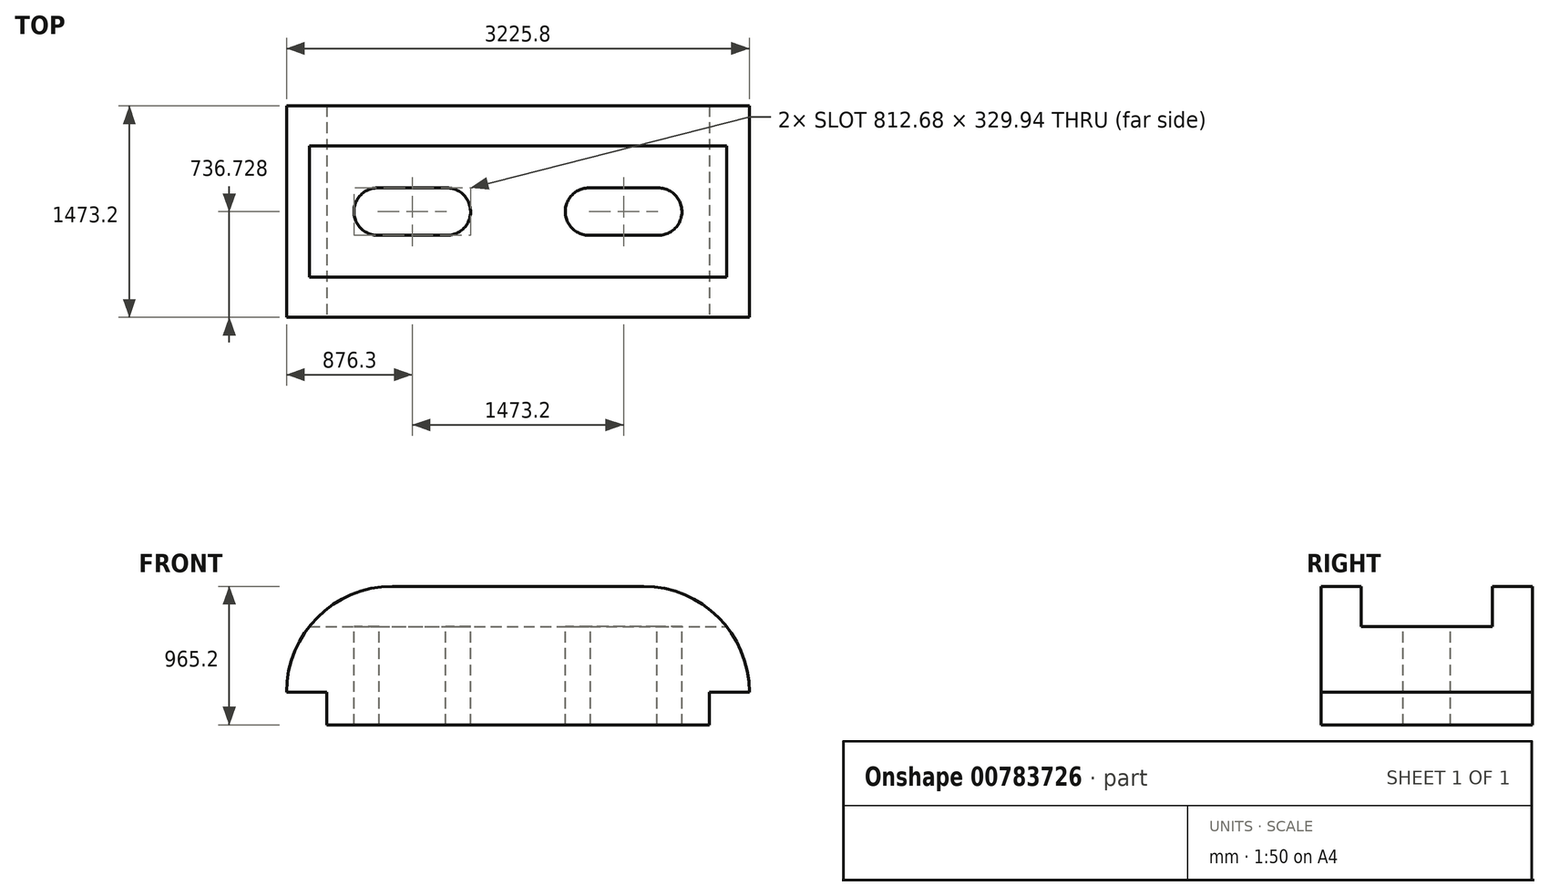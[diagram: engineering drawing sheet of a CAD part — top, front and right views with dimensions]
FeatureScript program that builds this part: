
annotation { "Feature Type Name" : "Feature", "Feature Type Description" : "" }
export const myFeature = defineFeature(function(context is Context, id is Id, definition is map)
    precondition{}
    {
        {
            var Q0;
            Q0=qCreatedBy(makeId("Front.planeOp"),FACE);
            var sketch = newSketch(context, id + "F0", { "sketchPlane" : qUnion([Q0])});
            skLineSegment(sketch, "E0.bottom", {"start": v(1612.9, 482.6) * mm, "end": v(-1612.9, 482.6) * mm});
            skLineSegment(sketch, "E0.top", {"start": v(1612.9, -482.6) * mm, "end": v(-1612.9, -482.6) * mm});
            skLineSegment(sketch, "E0.left", {"start": v(1612.9, 482.6) * mm, "end": v(1612.9, -482.6) * mm});
            skLineSegment(sketch, "E0.right", {"start": v(-1612.9, 482.6) * mm, "end": v(-1612.9, -482.6) * mm});
            skPoint(sketch, "E0.middle", {"position": v(0, 0) * mm});
            skSolve(sketch);
        }
        {
            var Q0;
            Q0=qSketchRegion(id+"F0",true);
            extrude(context, id + "F1", {"entities" : qUnion([Q0]), "depth" : 1473.2 * mm});
        }
        {
            var Q0;
            Q0=makeQuery(id+"F1.opExtrude","SWEPT_FACE",FACE,{"disambiguationData":[OSD([sQuery(id+"F0.wireOp",EDGE,"E0.bottom")])]});
            var sketch = newSketch(context, id + "F2", { "sketchPlane" : qUnion([Q0])});
            skArc(sketch, "E1", {"start": v(-977.59, -571.5) * mm, "mid": v(-1142.94, -741.04) * mm, "end": v(-968.7, -901.44) * mm});
            skPoint(sketch, "E1.centerSnap0", {"position": v(-1612.9, -736.6) * mm});
            skArc(sketch, "E2", {"start": v(-504.5, -901.44) * mm, "mid": v(-330.26, -741.04) * mm, "end": v(-495.61, -571.5) * mm});
            skLineSegment(sketch, "E3", {"start": v(-977.59, -571.5) * mm, "end": v(-494.99, -571.5) * mm});
            skLineSegment(sketch, "E4", {"start": v(-968.7, -901.44) * mm, "end": v(-486.1, -901.44) * mm});
            skLineSegment(sketch, "E5.MirrorCS", {"start": v(977.59, -571.5) * mm, "end": v(494.99, -571.5) * mm});
            skArc(sketch, "E6.MirrorCS", {"start": v(977.59, -571.5) * mm, "mid": v(1142.94, -741.04) * mm, "end": v(968.7, -901.44) * mm});
            skLineSegment(sketch, "E7.MirrorCS", {"start": v(968.7, -901.44) * mm, "end": v(486.1, -901.44) * mm});
            skArc(sketch, "E8.MirrorCS", {"start": v(504.5, -901.44) * mm, "mid": v(330.26, -741.04) * mm, "end": v(495.61, -571.5) * mm});
            skSolve(sketch);
        }
        {
            var Q0;
            Q0=qSketchRegion(id+"F2",true);
            extrude(context, id + "F3", {"entities" : qUnion([Q0]), "operationType" : NewBodyOperationType.REMOVE, "endBound" : BoundingType.THROUGH_ALL, "oppositeDirection" : true, "depth" : 25.4 * mm});
        }
        {
            var Q0;
            Q0=makeQuery(id+"F1.opExtrude","SWEPT_FACE",FACE,{"disambiguationData":[OSD([sQuery(id+"F0.wireOp",EDGE,"E0.left")])]});
            var sketch = newSketch(context, id + "F4", { "sketchPlane" : qUnion([Q0])});
            skLineSegment(sketch, "E9.bottom", {"start": v(-1193.8, 482.6) * mm, "end": v(-279.4, 482.6) * mm});
            skLineSegment(sketch, "E9.top", {"start": v(-1193.8, 203.2) * mm, "end": v(-279.4, 203.2) * mm});
            skLineSegment(sketch, "E9.left", {"start": v(-1193.8, 482.6) * mm, "end": v(-1193.8, 203.2) * mm});
            skLineSegment(sketch, "E9.right", {"start": v(-279.4, 482.6) * mm, "end": v(-279.4, 203.2) * mm});
            skSolve(sketch);
        }
        {
            var Q0;
            Q0=qSketchRegion(id+"F4",true);
            extrude(context, id + "F5", {"entities" : qUnion([Q0]), "operationType" : NewBodyOperationType.REMOVE, "endBound" : BoundingType.THROUGH_ALL, "oppositeDirection" : true, "depth" : 25.4 * mm});
        }
        {
            var Q0;
            Q0=makeQuery(id+"F1.opExtrude","CAP_FACE",FACE,{"disambiguationData":[OSD([sQuery(id+"F0.wireOp",EDGE,"E0.bottom"),sQuery(id+"F0.wireOp",EDGE,"E0.top"),sQuery(id+"F0.wireOp",EDGE,"E0.left"),sQuery(id+"F0.wireOp",EDGE,"E0.right")])],"isStart":false});
            var sketch = newSketch(context, id + "F6", { "sketchPlane" : qUnion([Q0])});
            skLineSegment(sketch, "E10.bottom", {"start": v(-1612.9, -482.6) * mm, "end": v(-1333.5, -482.6) * mm});
            skLineSegment(sketch, "E10.top", {"start": v(-1612.9, -254) * mm, "end": v(-1333.5, -254) * mm});
            skLineSegment(sketch, "E10.left", {"start": v(-1612.9, -482.6) * mm, "end": v(-1612.9, -254) * mm});
            skLineSegment(sketch, "E10.right", {"start": v(-1333.5, -482.6) * mm, "end": v(-1333.5, -254) * mm});
            skLineSegment(sketch, "E11", {"start": v(0, -482.6) * mm, "end": v(0, 482.6) * mm, "construction": true});
            skLineSegment(sketch, "E12.MirrorCS", {"start": v(1333.5, -482.6) * mm, "end": v(1333.5, -254) * mm});
            skLineSegment(sketch, "E13.MirrorCS", {"start": v(1612.9, -254) * mm, "end": v(1333.5, -254) * mm});
            skLineSegment(sketch, "E14.MirrorCS", {"start": v(1612.9, -482.6) * mm, "end": v(1612.9, -254) * mm});
            skLineSegment(sketch, "E15.MirrorCS", {"start": v(1612.9, -482.6) * mm, "end": v(1333.5, -482.6) * mm});
            skSolve(sketch);
        }
        {
            var Q0;
            Q0=qSketchRegion(id+"F6",true);
            extrude(context, id + "F7", {"entities" : qUnion([Q0]), "operationType" : NewBodyOperationType.REMOVE, "endBound" : BoundingType.THROUGH_ALL, "oppositeDirection" : true, "depth" : 25.4 * mm});
        }
        {
            var Q0;
            {var subQ0=sQuery(id+"F0.wireOp",EDGE,"E0.bottom");var subQ1=sQuery(id+"F0.wireOp",EDGE,"E0.right");Q0=makeQuery(id+"F5.boolean.opBoolean","SPLIT",EDGE,{"disambiguationData":[TD([makeQuery(id+"F5.opExtrude","SWEPT_FACE",FACE,{"disambiguationData":[OSD([sQuery(id+"F4.wireOp",EDGE,"E9.left")])]})])],"derivedFrom":makeQuery(id+"F1.opExtrude","SWEPT_EDGE",EDGE,{"disambiguationData":[OSD([subQ0,subQ1])]})});}
            var Q1;
            {var subQ0=sQuery(id+"F0.wireOp",EDGE,"E0.bottom");var subQ1=sQuery(id+"F0.wireOp",EDGE,"E0.left");Q1=makeQuery(id+"F5.boolean.opBoolean","SPLIT",EDGE,{"disambiguationData":[TD([makeQuery(id+"F5.opExtrude","SWEPT_FACE",FACE,{"disambiguationData":[OSD([sQuery(id+"F4.wireOp",EDGE,"E9.left")])]})])],"derivedFrom":makeQuery(id+"F1.opExtrude","SWEPT_EDGE",EDGE,{"disambiguationData":[OSD([subQ0,subQ1])]})});}
            fillet(context, id + "F8", {"entities" : qUnion([Q0, Q1]), "radius" : 736.6 * mm, "tangentPropagation" : true, "allowEdgeOverflow" : false});
        }
    });
